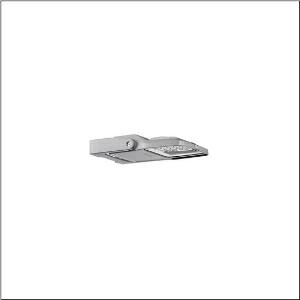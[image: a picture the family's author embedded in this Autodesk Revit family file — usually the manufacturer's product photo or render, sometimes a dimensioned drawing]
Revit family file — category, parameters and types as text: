
# Revit family: floodlight_fl_21_iq_micro___pl43_5xa7762a4a2a_306a
name_source: partatom
category: Lighting Fixtures
units: mm (PartAtom-declared; Revit-internal decimal feet)

## family parameters
Cut with Voids When Loaded = No
Host = Face
Light Source = No
Part Type = Normal
Room Calculation Point = No
Round Connector Dimension = Use Diameter
Shared = No

## types (1)
- --- (1 x LED, 3170 lm, 23.1 W, 4000K)
    Apparent Load = 23 VA
    CIE Flux Codes = 29 80 99 100 100
    Color Rendering = 70
    Color Temperature = 4000K
    Default Elevation = 1800 mm
    Description = Floodlight FL 21 iQ micro, floodlight, primary light control with lens, of PMMA, primary optical cover: protective disc, of toughened safety glass, transparent, light distribution: PL43, light emission: direct distribution, installation type: surface-mounted, LED, High Power LED, rated luminous flux: 3.170lm, luminous efficacy: 137lm/W, light colour: 740, colour temperature: 4000K, control: Auto-Match, Temp-Guard, Night-Set, Smart-Wire, Desk-Remote (wireless, voltage-free reading and setting of iQ features in the workshop via application-optimized NFC function/RFID function), optimised constant luminous flux control (CLO 2.0), Street-Remote, with terminal, 6-pole, mains connection: 220..240V, AC, 50/60Hz, start of lifetime: 23W, end of service life: 24W, reduction: 11W, luminaire housing, of diecast aluminium, powder-coated, Siteco® metallic grey (DB 702S), corrosivity category C5 mid according to DIN EN ISO 12944, sealing non-destructively replaceable, design bracket, of diecast aluminium, powder-coated, Siteco® metallic grey (DB 702S), protection rating (complete): IP66, insulation class (complete): insulation class II (safety insulation), certification: CE, ENEC, VDE, protection symbol: D, impact resistance: IK07, permissible operating ambient temperature: -40..+40°C, permissible operating ambient temperature for outdoor applications: -40..+50°C, standard: DIN EN 12944, LABS conformity tested according to VDMA 24364:2018-05, packaging unit: 1 piece

Light Distribution: PL43
    Height = 65 mm
    Lamp = 1 x LED
    Lamp Light Flux = 3170 lm
    Lamp Power = 23.1 W
    Lamp count = 1
    Length = 312 mm
    Luminous efficacy = 137 lm/W
    Manufacturer = Siteco
    ModVariant = No
    Model = 5XA7762A4A2A
    Mounting Place = Wall
    Mounting Type = Surface mounted
    Number of Poles = 1
    OnlyDefault = Yes
    Power Factor = 1
    Product Name = Floodlight FL 21 iQ micro | PL43
    Product group = floodlight | wall mounted
    ProductGroupID = 2001
    Protection Class = Protection class II
    Protection Degree = IP 66
    RLX_Detail_Level = 1
    RLX_Emergency_Light_Flux = 0 lm
    RLX_Emergency_Type = 0
    RLX_Emergency_Type_DB = No
    RlxData = <blob elided: 97161 chars, md5=c5a4193d>
    Socket = socket
    Standby Power = 0 W
    System Light Flux = 3170 lm
    System Power = 23 W
    Type Comments = factory setting: luminous flux: 100 % | dim-lin: 254 | 455 mA
    Type Image = l_1006878.jpg
    URL = http://relux.com
    VarID = @adj_127667
    Voltage = 0 V
    Weight = 0.00 kg
    Width = 230 mm

## geometry (parser evidence)
native form markers: Blend x4, Sweep x12
no freeform markers — native parametric forms only
